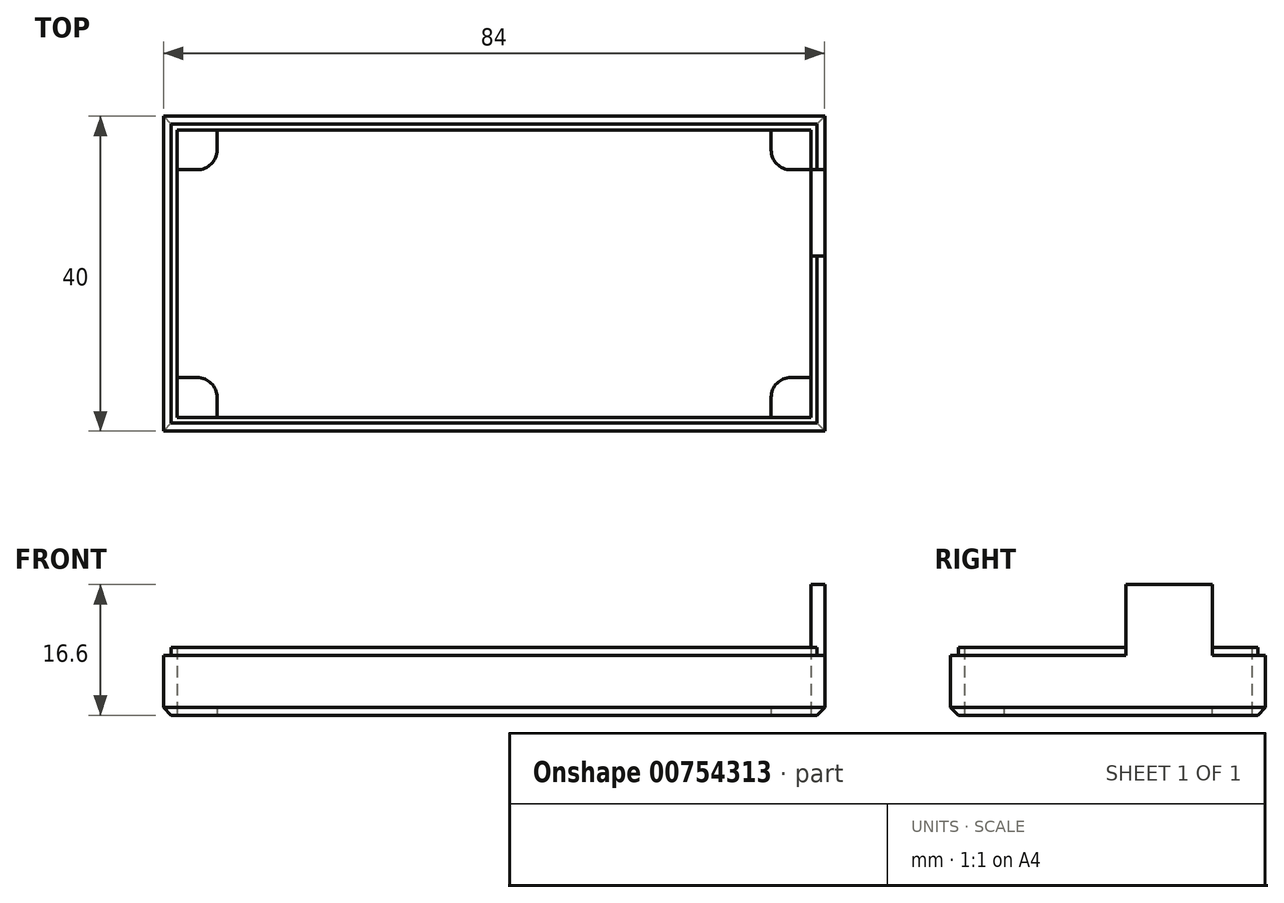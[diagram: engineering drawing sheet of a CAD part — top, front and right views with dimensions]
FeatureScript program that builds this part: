
annotation { "Feature Type Name" : "Feature", "Feature Type Description" : "" }
export const myFeature = defineFeature(function(context is Context, id is Id, definition is map)
    precondition{}
    {
        {
            var Q0;
            Q0=qCreatedBy(makeId("Top.planeOp"),FACE);
            var sketch = newSketch(context, id + "F0", { "sketchPlane" : qUnion([Q0])});
            skLineSegment(sketch, "E0.bottom", {"start": v(-40.58, 18.44) * mm, "end": v(39.92, 18.44) * mm});
            skLineSegment(sketch, "E0.top", {"start": v(-40.58, -18.06) * mm, "end": v(39.92, -18.06) * mm});
            skLineSegment(sketch, "E0.left", {"start": v(-40.58, 18.44) * mm, "end": v(-40.58, -18.06) * mm});
            skLineSegment(sketch, "E0.right", {"start": v(39.92, 18.44) * mm, "end": v(39.92, -18.06) * mm});
            skCircle(sketch, "E1", {"center": v(-38.03, 15.9) * mm, "radius": 1.45 * mm});
            skLineSegment(sketch, "E2", {"start": v(-0.33, 18.44) * mm, "end": v(-0.33, -18.06) * mm, "construction": true});
            skLineSegment(sketch, "E3", {"start": v(-40.58, 0.2) * mm, "end": v(39.92, 0.2) * mm, "construction": true});
            skLineSegment(sketch, "E4.bottom", {"start": v(-42.33, 20.2) * mm, "end": v(41.67, 20.2) * mm});
            skLineSegment(sketch, "E4.top", {"start": v(-42.33, -19.81) * mm, "end": v(41.67, -19.81) * mm});
            skLineSegment(sketch, "E4.left", {"start": v(-42.33, 20.2) * mm, "end": v(-42.33, -19.8) * mm});
            skLineSegment(sketch, "E4.right", {"start": v(41.67, 20.2) * mm, "end": v(41.67, -19.81) * mm});
            skArc(sketch, "E5", {"start": v(-35.53, 15.9) * mm, "mid": v(-36.26, 14.12) * mm, "end": v(-38.03, 13.4) * mm});
            skLineSegment(sketch, "E6", {"start": v(-35.53, 15.89) * mm, "end": v(-35.53, 18.44) * mm});
            skLineSegment(sketch, "E7", {"start": v(-38.03, 13.4) * mm, "end": v(-40.58, 13.4) * mm});
            skCircle(sketch, "E8.MirrorC", {"center": v(37.37, 15.9) * mm, "radius": 1.45 * mm});
            skLineSegment(sketch, "E9.MirrorCS", {"start": v(34.87, 15.9) * mm, "end": v(34.87, 18.44) * mm});
            skLineSegment(sketch, "E10.MirrorCS", {"start": v(37.37, 13.4) * mm, "end": v(39.92, 13.4) * mm});
            skArc(sketch, "E11.MirrorCS", {"start": v(34.87, 15.9) * mm, "mid": v(35.6, 14.12) * mm, "end": v(37.37, 13.4) * mm});
            skCircle(sketch, "E12.MirrorC", {"center": v(37.37, -15.51) * mm, "radius": 1.45 * mm});
            skLineSegment(sketch, "E13.MirrorCS", {"start": v(37.37, -13.01) * mm, "end": v(39.92, -13.01) * mm});
            skArc(sketch, "E14.MirrorCS", {"start": v(34.87, -15.51) * mm, "mid": v(35.6, -13.74) * mm, "end": v(37.37, -13.01) * mm});
            skLineSegment(sketch, "E15.MirrorCS", {"start": v(34.87, -15.5) * mm, "end": v(34.87, -18.06) * mm});
            skCircle(sketch, "E16.MirrorC", {"center": v(-38.03, -15.5) * mm, "radius": 1.45 * mm});
            skLineSegment(sketch, "E17.MirrorCS", {"start": v(-35.53, -15.5) * mm, "end": v(-35.53, -18.06) * mm});
            skLineSegment(sketch, "E18.MirrorCS", {"start": v(-38.03, -13) * mm, "end": v(-40.58, -13) * mm});
            skArc(sketch, "E19.MirrorCS", {"start": v(-35.53, -15.5) * mm, "mid": v(-36.26, -13.74) * mm, "end": v(-38.03, -13) * mm});
            skPoint(sketch, "E20.0.midPoint", {"position": v(39.84, 14.47) * mm});
            skPoint(sketch, "E21.0.midPoint", {"position": v(39.84, -16.94) * mm});
            skPoint(sketch, "E22.0.midPoint", {"position": v(-35.56, -16.93) * mm});
            skPoint(sketch, "E23.0.midPoint", {"position": v(-35.56, 14.47) * mm});
            skSolve(sketch);
        }
        {
            var Q0;
            Q0=makeQuery(id+"F0.imprint","IMPRINT",FACE,{"disambiguationData":[TD([[makeQuery(id+"F0.imprint","IMPRINT",EDGE,{"derivedFrom":sQuery(id+"F0.wireOp",EDGE,"E1")}),-1.0]])]});
            var Q1;
            Q1=makeQuery(id+"F0.imprint","IMPRINT",FACE,{"disambiguationData":[TD([[makeQuery(id+"F0.imprint","IMPRINT",EDGE,{"derivedFrom":sQuery(id+"F0.wireOp",EDGE,"E8.MirrorC")}),1.0]])]});
            var Q2;
            Q2=makeQuery(id+"F0.imprint","IMPRINT",FACE,{"disambiguationData":[TD([[makeQuery(id+"F0.imprint","IMPRINT",EDGE,{"derivedFrom":sQuery(id+"F0.wireOp",EDGE,"E16.MirrorC")}),1.0]])]});
            var Q3;
            Q3=makeQuery(id+"F0.imprint","IMPRINT",FACE,{"disambiguationData":[TD([[makeQuery(id+"F0.imprint","IMPRINT",EDGE,{"derivedFrom":sQuery(id+"F0.wireOp",EDGE,"E12.MirrorC")}),-1.0]])]});
            var Q4;
            Q4=makeQuery(id+"F0.imprint","IMPRINT",FACE,{"disambiguationData":[TD([[makeQuery(id+"F0.imprint","IMPRINT",EDGE,{"derivedFrom":sQuery(id+"F0.wireOp",EDGE,"E4.bottom")}),-1.0]])]});
            var Q5;
            Q5=makeQuery(id+"F0.imprint","IMPRINT",FACE,{"disambiguationData":[TD([[makeQuery(id+"F0.imprint","IMPRINT",EDGE,{"derivedFrom":sQuery(id+"F0.wireOp",EDGE,"E5")}),1.0]])]});
            var Q6;
            Q6=makeQuery(id+"F0.imprint","IMPRINT",FACE,{"disambiguationData":[TD([[makeQuery(id+"F0.imprint","IMPRINT",EDGE,{"derivedFrom":sQuery(id+"F0.wireOp",EDGE,"E1")}),1.0]])]});
            var Q7;
            Q7=makeQuery(id+"F0.imprint","IMPRINT",FACE,{"disambiguationData":[TD([[makeQuery(id+"F0.imprint","IMPRINT",EDGE,{"derivedFrom":sQuery(id+"F0.wireOp",EDGE,"E16.MirrorC")}),-1.0]])]});
            var Q8;
            Q8=makeQuery(id+"F0.imprint","IMPRINT",FACE,{"disambiguationData":[TD([[makeQuery(id+"F0.imprint","IMPRINT",EDGE,{"derivedFrom":sQuery(id+"F0.wireOp",EDGE,"E8.MirrorC")}),-1.0]])]});
            var Q9;
            Q9=makeQuery(id+"F0.imprint","IMPRINT",FACE,{"disambiguationData":[TD([[makeQuery(id+"F0.imprint","IMPRINT",EDGE,{"derivedFrom":sQuery(id+"F0.wireOp",EDGE,"E12.MirrorC")}),1.0]])]});
            extrude(context, id + "F1", {"entities" : qUnion([Q0, Q1, Q2, Q3, Q4, Q5, Q6, Q7, Q8, Q9]), "depth" : 1 * mm, "offsetDistance" : 25 * mm});
        }
        {
            var Q0;
            Q0=makeQuery(id+"F0.imprint","IMPRINT",FACE,{"disambiguationData":[TD([[makeQuery(id+"F0.imprint","IMPRINT",EDGE,{"derivedFrom":sQuery(id+"F0.wireOp",EDGE,"E4.bottom")}),-1.0]])]});
            extrude(context, id + "F2", {"entities" : qUnion([Q0]), "operationType" : NewBodyOperationType.ADD, "depth" : 7.6 * mm, "offsetDistance" : 25 * mm});
        }
        {
            var Q0;
            Q0=makeQuery(id+"F2.opExtrude","CAP_FACE",FACE,{"disambiguationData":[OSD([sQuery(id+"F0.wireOp",EDGE,"E0.bottom"),sQuery(id+"F0.wireOp",EDGE,"E0.top"),sQuery(id+"F0.wireOp",EDGE,"E0.left"),sQuery(id+"F0.wireOp",EDGE,"E0.right"),sQuery(id+"F0.wireOp",EDGE,"E4.bottom"),sQuery(id+"F0.wireOp",EDGE,"E4.top"),sQuery(id+"F0.wireOp",EDGE,"E4.left"),sQuery(id+"F0.wireOp",EDGE,"E4.right")])],"isStart":false});
            var sketch = newSketch(context, id + "F3", { "sketchPlane" : qUnion([Q0])});
            skLineSegment(sketch, "E24.bottom", {"start": v(-41.33, 19.19) * mm, "end": v(40.67, 19.19) * mm});
            skLineSegment(sketch, "E24.top", {"start": v(-41.33, -18.8) * mm, "end": v(40.67, -18.8) * mm});
            skLineSegment(sketch, "E24.left", {"start": v(-41.33, 19.19) * mm, "end": v(-41.33, -18.8) * mm});
            skLineSegment(sketch, "E24.right", {"start": v(40.67, 19.19) * mm, "end": v(40.67, -18.8) * mm});
            skSolve(sketch);
        }
        {
            var Q0;
            Q0=makeQuery(id+"F3.imprint","IMPRINT",FACE,{"disambiguationData":[TD([[makeQuery(id+"F3.imprint","IMPRINT",EDGE,{"derivedFrom":sQuery(id+"F3.wireOp",EDGE,"E24.bottom")}),-1.0]])]});
            extrude(context, id + "F4", {"entities" : qUnion([Q0]), "operationType" : NewBodyOperationType.ADD, "depth" : 1 * mm, "offsetDistance" : 25 * mm});
        }
        {
            var Q0;
            Q0=makeQuery(id+"F0.imprint","IMPRINT",FACE,{"disambiguationData":[TD([[makeQuery(id+"F0.imprint","IMPRINT",EDGE,{"derivedFrom":sQuery(id+"F0.wireOp",EDGE,"E5")}),1.0]])]});
            var sketch = newSketch(context, id + "F5", { "sketchPlane" : qUnion([Q0])});
            skLineSegment(sketch, "E25.bottom", {"start": v(-34.33, -9.8) * mm, "end": v(33.67, -9.8) * mm});
            skLineSegment(sketch, "E25.top", {"start": v(-34.33, 10.2) * mm, "end": v(33.67, 10.2) * mm});
            skLineSegment(sketch, "E25.left", {"start": v(-34.33, -9.8) * mm, "end": v(-34.33, 10.2) * mm});
            skLineSegment(sketch, "E25.right", {"start": v(33.67, -9.8) * mm, "end": v(33.67, 10.2) * mm});
            skSolve(sketch);
        }
        {
            var Q0;
            Q0=makeQuery(id+"F5.imprint","IMPRINT",FACE,{"disambiguationData":[TD([[makeQuery(id+"F5.imprint","IMPRINT",EDGE,{"derivedFrom":sQuery(id+"F5.wireOp",EDGE,"E25.bottom")}),1.0]])]});
            extrude(context, id + "F6", {"entities" : qUnion([Q0]), "operationType" : NewBodyOperationType.REMOVE, "oppositeDirection" : true, "depth" : -5 * mm, "offsetDistance" : 25 * mm});
        }
        {
            var Q0;
            {var subQ0=sQuery(id+"F0.wireOp",EDGE,"E4.right");Q0=makeQuery(id+"F2.boolean.opBoolean","MERGE",FACE,{"derivedFrom":[makeQuery(id+"F1.opExtrude","SWEPT_FACE",FACE,{"disambiguationData":[OSD([subQ0])]}),makeQuery(id+"F2.opExtrude","SWEPT_FACE",FACE,{"disambiguationData":[OSD([subQ0])]})]});}
            var sketch = newSketch(context, id + "F7", { "sketchPlane" : qUnion([Q0])});
            skLineSegment(sketch, "E26.bottom", {"start": v(13.44, 16.6) * mm, "end": v(2.44, 16.6) * mm});
            skLineSegment(sketch, "E26.top", {"start": v(13.44, 2.95) * mm, "end": v(2.44, 2.95) * mm});
            skLineSegment(sketch, "E26.left", {"start": v(13.44, 16.6) * mm, "end": v(13.44, 2.95) * mm});
            skLineSegment(sketch, "E26.right", {"start": v(2.44, 16.6) * mm, "end": v(2.44, 2.95) * mm});
            skSolve(sketch);
        }
        {
            var Q0;
            Q0 = qSketchRegion(id + "F7", true);
            extrude(context, id + "F8", {"entities" : qUnion([Q0]), "operationType" : NewBodyOperationType.ADD, "oppositeDirection" : true, "depth" : 1.75 * mm, "offsetDistance" : 25 * mm});
        }
        {
            var Q0;
            Q0=makeQuery(id+"F1.opExtrude","CAP_EDGE",EDGE,{"disambiguationData":[OSD([sQuery(id+"F0.wireOp",EDGE,"E4.top")])],"isStart":true});
            var Q1;
            Q1=makeQuery(id+"F1.opExtrude","CAP_EDGE",EDGE,{"disambiguationData":[OSD([sQuery(id+"F0.wireOp",EDGE,"E4.right")])],"isStart":true});
            var Q2;
            Q2=makeQuery(id+"F1.opExtrude","CAP_EDGE",EDGE,{"disambiguationData":[OSD([sQuery(id+"F0.wireOp",EDGE,"E4.bottom")])],"isStart":true});
            var Q3;
            Q3=makeQuery(id+"F1.opExtrude","CAP_EDGE",EDGE,{"disambiguationData":[OSD([sQuery(id+"F0.wireOp",EDGE,"E4.left")])],"isStart":true});
            chamfer(context, id + "F9", {"entities" : qUnion([Q0, Q1, Q2, Q3]), "width" : 1 * mm, "tangentPropagation" : true});
        }
    });
